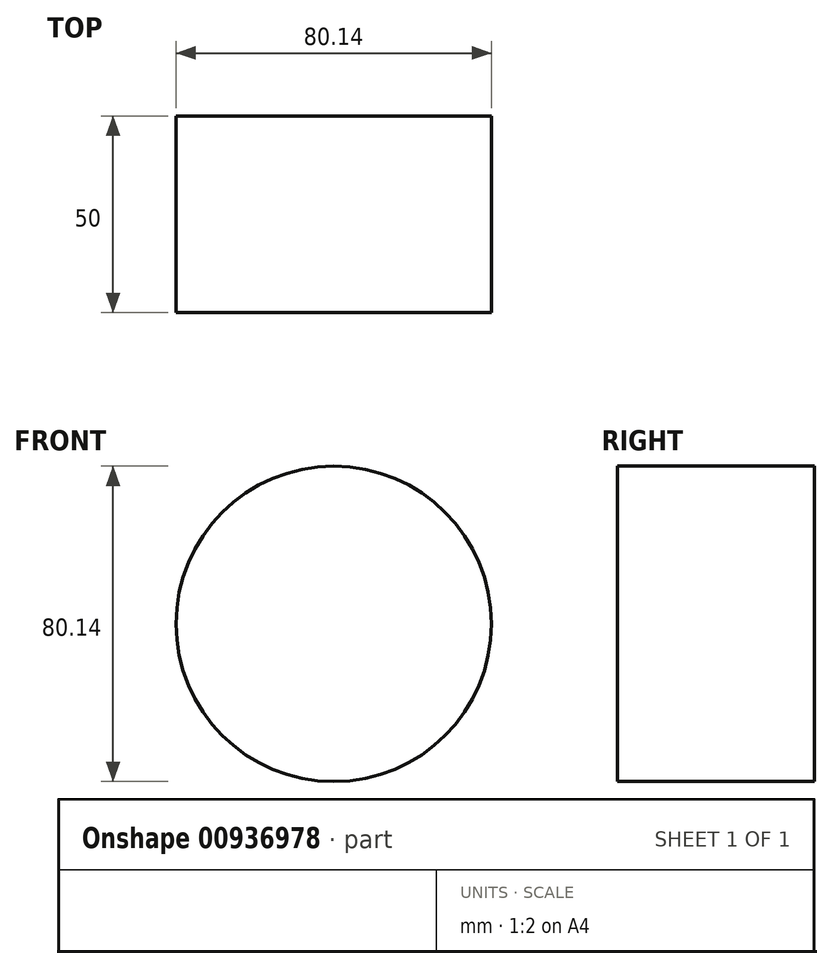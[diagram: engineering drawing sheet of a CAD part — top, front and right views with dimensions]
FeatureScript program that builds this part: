
annotation { "Feature Type Name" : "Feature", "Feature Type Description" : "" }
export const myFeature = defineFeature(function(context is Context, id is Id, definition is map)
    precondition{}
    {
        {
            var Q0;
            Q0=qCreatedBy(makeId("Front.planeOp"),FACE);
            var sketch = newSketch(context, id + "F0", { "sketchPlane" : qUnion([Q0])});
            skCircle(sketch, "E0", {"center": v(0, 0) * mm, "radius": 40.07 * mm});
            skSolve(sketch);
        }
        {
            var Q0;
            Q0=makeQuery(id+"F0.imprint","IMPRINT",FACE,{"disambiguationData":[TD([[makeQuery(id+"F0.imprint","IMPRINT",EDGE,{"derivedFrom":sQuery(id+"F0.wireOp",EDGE,"E0")}),1.0]])]});
            extrude(context, id + "F1", {"entities" : qUnion([Q0]), "depth" : 25 * mm, "offsetDistance" : 25 * mm, "hasSecondDirection" : true, "secondDirectionOppositeDirection" : true, "secondDirectionDepth" : 25 * mm});
        }
    });
